# Revit family: VT CM 30 2P
name_source: partatom
category: Specialty Equipment
revit_build: Autodesk Revit 2017 (Build: 20160225_1515(x64)
units: mm (PartAtom-declared; Revit-internal decimal feet)

## family parameters
Cut with Voids When Loaded = No
Host = Face
Part Type = Normal
Room Calculation Point = No
Round Connector Dimension = Use Diameter
Shared = No

## types (1)
- VT CM 30 2P
    Alto encastre = -80 mm
    Ancho Encastre = 280 mm  [stored 0.918635 ft]
    Ca_1_Cable Conexión Tri-fásica = Yes
    Ca_1_Cable de conexión = 900 mm
    Ca_1_Frecuencia Hz. = 50/60
    Ca_1_Potencia nominal max. W. = 3000
    Ca_2_Doble circuito High light Ø 120/180 = _
    Ca_2_Doble circuito High light Ø 120/210 = -
    Ca_2_Doble circuito High light Ø 180/210 = _
    Ca_2_Elemento calefactor grill 200x235/2.500 W = -
    Ca_2_High light Ø 145 = 1
    Ca_2_High light Ø 160 = _
    Ca_2_High light Ø 180 = 1
    Ca_2_High light Ø 210 = _
    Ca_2_Inducción Oval = -
    Ca_2_Inducción ø 145 = -
    Ca_2_Inducción ø 160 = -
    Ca_2_Inducción ø 180 = -
    Ca_2_Inducción ø 210 = -
    Ca_2_Inducción ø 210, 3.200 = -
    Ca_2_Inducción ø 250 = -
    Ca_2_Inducción ø 280 = -
    Ca_2_Rápida Ø 145 = _
    Ca_2_Rápida Ø 180 = -
    Ca_2_Triple circuito High light Ø 145/210/270 = -
    Ca_3_Detector de recipientes = No
    Ca_3_Función Power Plus = No
    Ca_3_Función Stop & Go = No
    Ca_3_Función cronómetro = 1
    Ca_3_Golpe de cocción = No
    Ca_3_Keep Warm = No
    Ca_3_Programador tiempo de cocción = No
    Ca_3_Touch control (Slider) = No
    Ca_4_Bloqueo de seguridad = No
    Ca_4_Desconexión automática de seguridad = Yes
    Ca_4_Indicador de calor residual = Yes
    Ca_5_Cristal Biselado = Yes
    Ca_5_Encimera de cantos redondeados = No
    Ca_5_Encimera rectangular = No
    Ca_5_Marco Inox = No
    Ca_Ancho = 300 mm
    Ca_Ancho Interior = 270 mm
    Ca_Certificación (Chile) = E-013-01-29993
    Ca_Creado por = Catálogo Arquitectura
    Ca_Código Catálogo Arquitectura = 465_TEK_034
    Ca_Código EAN = 8421152060407
    Ca_Código del Producto = 10208049
    Ca_Especificaciones Técnicas = Encimera por inducción empotrable para cocina modelo VT CM 30 2P
    Ca_Fabricante = Teka
    Ca_Instalación = Empotrable
    Ca_Itemizado CDT = E 08 06 02
    Ca_Masterformat = 11 30 13.13
    Ca_Material Principal = Cristal templado de alta seguridad
    Ca_Medidas de embalaje = 36 x 57 x 10
    Ca_País de Fabricación = Turquía
    Ca_Peso = 5,2 kg
    Ca_Producto = Encimera inducción VT CM 30 2P
    Ca_Profundidad = 520 mm
    Ca_Profundidad Interior = 500 mm
    Ca_Representante = Teka
    Ca_Teléfono = 99821 1017
    Ca_Usos = Encimera por inducción empotrable para mueble de cocina
    Ca_Web del Fabricante = www.teka.cl
    Ca_Web del Representante = www.teka.cl
    Cubierta encimera = Teka_Panel Negro
    Default Elevation = 1219.2 mm  [stored 4 ft]
    Description = Encimera por inducción empotrable para mueble de cocina
    Disco Inducción = Teka_Interior Negro
    Encimera Vidrio = Teka_Panel Vidrio
    Interior encimera = Teka_Aluminio
    Luz encendido = Teka_Menu Luz Roja
    Manufacturer = Teka
    Model = VT CM 30 2P
    Profundiadad encimera = 40 mm
    Profundidad encastre = 490 mm
    URL = www.teka.cl
    Voltage = 220/240 V
    Wattage = 3000

note: [stored X ft] marks values corroborated as IEEE doubles in the binary element streams (Revit-internal decimal feet)

## geometry (parser evidence)
native form markers: Sweep x6
no freeform markers — native parametric forms only
